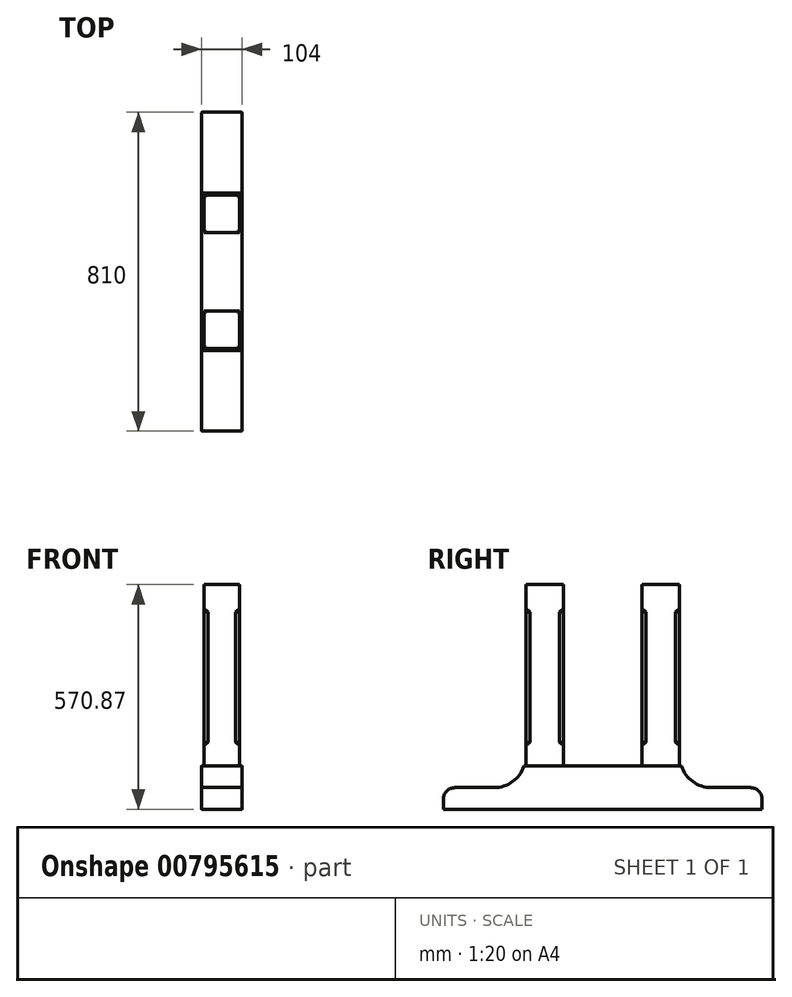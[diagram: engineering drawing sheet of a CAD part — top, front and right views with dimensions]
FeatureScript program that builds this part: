
annotation { "Feature Type Name" : "Feature", "Feature Type Description" : "" }
export const myFeature = defineFeature(function(context is Context, id is Id, definition is map)
    precondition{}
    {
        {
            var Q0;
            Q0=qCreatedBy(makeId("Right.planeOp"),FACE);
            var sketch = newSketch(context, id + "F0", { "sketchPlane" : qUnion([Q0])});
            skLineSegment(sketch, "E0", {"start": v(-405, 0) * mm, "end": v(-405, 55) * mm});
            skLineSegment(sketch, "E1", {"start": v(-405, 55) * mm, "end": v(-200, 55) * mm});
            skLineSegment(sketch, "E2", {"start": v(-200, 55) * mm, "end": v(-200, 110) * mm});
            skLineSegment(sketch, "E3", {"start": v(-200, 110) * mm, "end": v(-195, 110) * mm});
            skLineSegment(sketch, "E4", {"start": v(-195, 110) * mm, "end": v(-195, 570.87) * mm});
            skLineSegment(sketch, "E5", {"start": v(-195, 570.87) * mm, "end": v(-100, 570.87) * mm});
            skLineSegment(sketch, "E6", {"start": v(-100, 570.87) * mm, "end": v(-100, 110) * mm});
            skLineSegment(sketch, "E7", {"start": v(-100, 110) * mm, "end": v(0, 110) * mm});
            skLineSegment(sketch, "E8.MirrorCS", {"start": v(405, 0) * mm, "end": v(405, 55) * mm});
            skLineSegment(sketch, "E9.MirrorCS", {"start": v(405, 55) * mm, "end": v(200, 55) * mm});
            skLineSegment(sketch, "E10.MirrorCS", {"start": v(200, 110) * mm, "end": v(195, 110) * mm});
            skLineSegment(sketch, "E11.MirrorCS", {"start": v(195, 110) * mm, "end": v(195, 570.87) * mm});
            skLineSegment(sketch, "E12.MirrorCS", {"start": v(195, 570.87) * mm, "end": v(100, 570.87) * mm});
            skLineSegment(sketch, "E13.MirrorCS", {"start": v(100, 570.87) * mm, "end": v(100, 110) * mm});
            skLineSegment(sketch, "E14.MirrorCS", {"start": v(100, 110) * mm, "end": v(0, 110) * mm});
            skLineSegment(sketch, "E15.MirrorCS", {"start": v(200, 55) * mm, "end": v(200, 110) * mm});
            skLineSegment(sketch, "E16", {"start": v(-405, 0) * mm, "end": v(405, 0) * mm});
            skLineSegment(sketch, "E17", {"start": v(-195, 110) * mm, "end": v(-100, 110) * mm});
            skLineSegment(sketch, "E18", {"start": v(100, 110) * mm, "end": v(195, 110) * mm});
            skSolve(sketch);
        }
        {
            var Q0;
            Q0=makeQuery(id+"F0.imprint","IMPRINT",FACE,{"disambiguationData":[TD([[makeQuery(id+"F0.imprint","IMPRINT",EDGE,{"derivedFrom":sQuery(id+"F0.wireOp",EDGE,"E0")}),-1.0]])]});
            extrude(context, id + "F1", {"entities" : qUnion([Q0]), "depth" : 52 * mm, "offsetDistance" : 25 * mm, "hasSecondDirection" : true, "secondDirectionOppositeDirection" : true, "secondDirectionDepth" : 52 * mm});
        }
        {
            var Q0;
            Q0=makeQuery(id+"F0.imprint","IMPRINT",FACE,{"disambiguationData":[TD([[makeQuery(id+"F0.imprint","IMPRINT",EDGE,{"derivedFrom":sQuery(id+"F0.wireOp",EDGE,"E4")}),-1.0]])]});
            var Q1;
            Q1=makeQuery(id+"F0.imprint","IMPRINT",FACE,{"disambiguationData":[TD([[makeQuery(id+"F0.imprint","IMPRINT",EDGE,{"derivedFrom":sQuery(id+"F0.wireOp",EDGE,"E11.MirrorCS")}),1.0]])]});
            extrude(context, id + "F2", {"entities" : qUnion([Q0, Q1]), "operationType" : NewBodyOperationType.ADD, "oppositeDirection" : true, "depth" : 45 * mm, "offsetDistance" : 25 * mm, "hasSecondDirection" : true, "secondDirectionOppositeDirection" : false, "secondDirectionDepth" : 45 * mm});
        }
        {
            var Q0;
            Q0=makeQuery(id+"F1.opExtrude","SWEPT_EDGE",EDGE,{"disambiguationData":[OSD([sQuery(id+"F0.wireOp",EDGE,"E9.MirrorCS"),sQuery(id+"F0.wireOp",EDGE,"E8.MirrorCS")])]});
            var Q1;
            Q1=makeQuery(id+"F1.opExtrude","SWEPT_EDGE",EDGE,{"disambiguationData":[OSD([sQuery(id+"F0.wireOp",EDGE,"E0"),sQuery(id+"F0.wireOp",EDGE,"E1")])]});
            fillet(context, id + "F3", {"entities" : qUnion([Q0, Q1]), "radius" : 30 * mm, "tangentPropagation" : true, "allowEdgeOverflow" : false});
        }
        {
            var Q0;
            Q0=makeQuery(id+"F1.opExtrude","SWEPT_EDGE",EDGE,{"disambiguationData":[OSD([sQuery(id+"F0.wireOp",EDGE,"E9.MirrorCS"),sQuery(id+"F0.wireOp",EDGE,"E15.MirrorCS")])]});
            fillet(context, id + "F4", {"entities" : qUnion([Q0]), "radius" : 80 * mm, "tangentPropagation" : true, "allowEdgeOverflow" : false});
        }
        {
            var Q0;
            Q0=makeQuery(id+"F1.opExtrude","SWEPT_EDGE",EDGE,{"disambiguationData":[OSD([sQuery(id+"F0.wireOp",EDGE,"E1"),sQuery(id+"F0.wireOp",EDGE,"E2")])]});
            fillet(context, id + "F5", {"entities" : qUnion([Q0]), "radius" : 80 * mm, "tangentPropagation" : true, "allowEdgeOverflow" : false});
        }
        {
            var Q0;
            Q0=makeQuery(id+"F2.opExtrude","CAP_EDGE",EDGE,{"disambiguationData":[OSD([sQuery(id+"F0.wireOp",EDGE,"E4")])],"isStart":true});
            var Q1;
            Q1=makeQuery(id+"F2.opExtrude","CAP_EDGE",EDGE,{"disambiguationData":[OSD([sQuery(id+"F0.wireOp",EDGE,"E6")])],"isStart":true});
            var Q2;
            Q2=makeQuery(id+"F2.opExtrude","CAP_EDGE",EDGE,{"disambiguationData":[OSD([sQuery(id+"F0.wireOp",EDGE,"E13.MirrorCS")])],"isStart":true});
            var Q3;
            Q3=makeQuery(id+"F2.opExtrude","CAP_EDGE",EDGE,{"disambiguationData":[OSD([sQuery(id+"F0.wireOp",EDGE,"E4")])],"isStart":false});
            var Q4;
            Q4=makeQuery(id+"F2.opExtrude","CAP_EDGE",EDGE,{"disambiguationData":[OSD([sQuery(id+"F0.wireOp",EDGE,"E6")])],"isStart":false});
            var Q5;
            Q5=makeQuery(id+"F2.opExtrude","CAP_EDGE",EDGE,{"disambiguationData":[OSD([sQuery(id+"F0.wireOp",EDGE,"E13.MirrorCS")])],"isStart":false});
            var Q6;
            Q6=makeQuery(id+"F2.opExtrude","CAP_EDGE",EDGE,{"disambiguationData":[OSD([sQuery(id+"F0.wireOp",EDGE,"E11.MirrorCS")])],"isStart":false});
            var Q7;
            Q7=makeQuery(id+"F2.opExtrude","CAP_EDGE",EDGE,{"disambiguationData":[OSD([sQuery(id+"F0.wireOp",EDGE,"E11.MirrorCS")])],"isStart":true});
            chamfer(context, id + "F6", {"entities" : qUnion([Q0, Q1, Q2, Q3, Q4, Q5, Q6, Q7]), "width" : 10 * mm, "tangentPropagation" : true});
        }
        {
            var Q0;
            Q0=makeQuery(id+"F1.opExtrude","SWEPT_FACE",FACE,{"disambiguationData":[OSD([sQuery(id+"F0.wireOp",EDGE,"E3"),sQuery(id+"F0.wireOp",EDGE,"E7"),sQuery(id+"F0.wireOp",EDGE,"E10.MirrorCS"),sQuery(id+"F0.wireOp",EDGE,"E14.MirrorCS"),sQuery(id+"F0.wireOp",EDGE,"E17"),sQuery(id+"F0.wireOp",EDGE,"E18")])]});
            var sketch = newSketch(context, id + "F7", { "sketchPlane" : qUnion([Q0])});
            skLineSegment(sketch, "E19.bottom", {"start": v(-45, -195) * mm, "end": v(45, -195) * mm});
            skLineSegment(sketch, "E19.top", {"start": v(-45, -100) * mm, "end": v(45, -100) * mm});
            skLineSegment(sketch, "E19.left", {"start": v(-45, -195) * mm, "end": v(-45, -100) * mm});
            skLineSegment(sketch, "E19.right", {"start": v(45, -195) * mm, "end": v(45, -100) * mm});
            skLineSegment(sketch, "E20.bottom", {"start": v(-45, 100) * mm, "end": v(45, 100) * mm});
            skLineSegment(sketch, "E20.top", {"start": v(-45, 195) * mm, "end": v(45, 195) * mm});
            skLineSegment(sketch, "E20.left", {"start": v(-45, 100) * mm, "end": v(-45, 195) * mm});
            skLineSegment(sketch, "E20.right", {"start": v(45, 100) * mm, "end": v(45, 195) * mm});
            skSolve(sketch);
        }
        {
            var Q0;
            Q0 = qSketchRegion(id + "F7", true);
            extrude(context, id + "F8", {"entities" : qUnion([Q0]), "operationType" : NewBodyOperationType.ADD, "depth" : 50 * mm, "offsetDistance" : 25 * mm});
        }
        {
            var Q0;
            Q0=makeQuery(id+"F2.opExtrude","SWEPT_FACE",FACE,{"disambiguationData":[OSD([sQuery(id+"F0.wireOp",EDGE,"E5")])]});
            var sketch = newSketch(context, id + "F9", { "sketchPlane" : qUnion([Q0])});
            skLineSegment(sketch, "E21.bottom", {"start": v(45, 195) * mm, "end": v(-45, 195) * mm});
            skLineSegment(sketch, "E21.top", {"start": v(45, 100) * mm, "end": v(-45, 100) * mm});
            skLineSegment(sketch, "E21.left", {"start": v(45, 195) * mm, "end": v(45, 100) * mm});
            skLineSegment(sketch, "E21.right", {"start": v(-45, 195) * mm, "end": v(-45, 100) * mm});
            skPoint(sketch, "E22.firstSnap0", {"position": v(45, -147.5) * mm});
            skLineSegment(sketch, "E22.bottom", {"start": v(45, -100) * mm, "end": v(-45, -100) * mm});
            skLineSegment(sketch, "E22.top", {"start": v(45, -195) * mm, "end": v(-45, -195) * mm});
            skLineSegment(sketch, "E22.left", {"start": v(45, -100) * mm, "end": v(45, -195) * mm});
            skLineSegment(sketch, "E22.right", {"start": v(-45, -100) * mm, "end": v(-45, -195) * mm});
            skSolve(sketch);
        }
        {
            var Q0;
            {var subQ1=makeQuery(id+"F6.opChamfer","BLEND_EDGE",EDGE,{"blendedFrom":[makeQuery(id+"F2.opExtrude","CAP_EDGE",EDGE,{"disambiguationData":[OSD([sQuery(id+"F0.wireOp",EDGE,"E6")])],"isStart":true}),makeQuery(id+"F2.opExtrude","SWEPT_FACE",FACE,{"disambiguationData":[OSD([sQuery(id+"F0.wireOp",EDGE,"E5")])]})],"blendedInto":[makeQuery(id+"F2.opExtrude","SWEPT_FACE",FACE,{"disambiguationData":[OSD([sQuery(id+"F0.wireOp",EDGE,"E5")])]})]});Q0=makeQuery(id+"F9.imprint","IMPRINT",FACE,{"disambiguationData":[TD([[makeQuery(id+"F9.imprint","IMPRINT",EDGE,{"derivedFrom":subQ1}),-1.0]])]});}
            var Q1;
            {var subQ1=makeQuery(id+"F6.opChamfer","BLEND_EDGE",EDGE,{"blendedFrom":[makeQuery(id+"F2.opExtrude","CAP_EDGE",EDGE,{"disambiguationData":[OSD([sQuery(id+"F0.wireOp",EDGE,"E6")])],"isStart":false}),makeQuery(id+"F2.opExtrude","SWEPT_FACE",FACE,{"disambiguationData":[OSD([sQuery(id+"F0.wireOp",EDGE,"E5")])]})],"blendedInto":[makeQuery(id+"F2.opExtrude","SWEPT_FACE",FACE,{"disambiguationData":[OSD([sQuery(id+"F0.wireOp",EDGE,"E5")])]})]});Q1=makeQuery(id+"F9.imprint","IMPRINT",FACE,{"disambiguationData":[TD([[makeQuery(id+"F9.imprint","IMPRINT",EDGE,{"derivedFrom":subQ1}),-1.0]])]});}
            var Q2;
            {var subQ1=makeQuery(id+"F6.opChamfer","BLEND_EDGE",EDGE,{"blendedFrom":[makeQuery(id+"F2.opExtrude","CAP_EDGE",EDGE,{"disambiguationData":[OSD([sQuery(id+"F0.wireOp",EDGE,"E4")])],"isStart":true}),makeQuery(id+"F2.opExtrude","SWEPT_FACE",FACE,{"disambiguationData":[OSD([sQuery(id+"F0.wireOp",EDGE,"E5")])]})],"blendedInto":[makeQuery(id+"F2.opExtrude","SWEPT_FACE",FACE,{"disambiguationData":[OSD([sQuery(id+"F0.wireOp",EDGE,"E5")])]})]});Q2=makeQuery(id+"F9.imprint","IMPRINT",FACE,{"disambiguationData":[TD([[makeQuery(id+"F9.imprint","IMPRINT",EDGE,{"derivedFrom":subQ1}),-1.0]])]});}
            var Q3;
            {var subQ1=makeQuery(id+"F6.opChamfer","BLEND_EDGE",EDGE,{"blendedFrom":[makeQuery(id+"F2.opExtrude","CAP_EDGE",EDGE,{"disambiguationData":[OSD([sQuery(id+"F0.wireOp",EDGE,"E4")])],"isStart":false}),makeQuery(id+"F2.opExtrude","SWEPT_FACE",FACE,{"disambiguationData":[OSD([sQuery(id+"F0.wireOp",EDGE,"E5")])]})],"blendedInto":[makeQuery(id+"F2.opExtrude","SWEPT_FACE",FACE,{"disambiguationData":[OSD([sQuery(id+"F0.wireOp",EDGE,"E5")])]})]});Q3=makeQuery(id+"F9.imprint","IMPRINT",FACE,{"disambiguationData":[TD([[makeQuery(id+"F9.imprint","IMPRINT",EDGE,{"derivedFrom":subQ1}),-1.0]])]});}
            var Q4;
            Q4=makeQuery(id+"F9.imprint","IMPRINT",FACE,{"disambiguationData":[TD([[makeQuery(id+"F9.imprint","IMPRINT",EDGE,{"derivedFrom":sQuery(id+"F9.wireOp",EDGE,"E21.bottom")}),1.0]])]});
            var Q5;
            {var subQ1=makeQuery(id+"F2.opExtrude","SWEPT_FACE",FACE,{"disambiguationData":[OSD([sQuery(id+"F0.wireOp",EDGE,"E5")])]});var subQ2=sQuery(id+"F0.wireOp",EDGE,"E4");var subQ7=makeQuery(id+"F6.opChamfer","BLEND_EDGE",EDGE,{"blendedFrom":[makeQuery(id+"F2.opExtrude","CAP_EDGE",EDGE,{"disambiguationData":[OSD([subQ2])],"isStart":true}),subQ1],"blendedInto":[subQ1]});Q5=makeQuery(id+"F9.imprint","IMPRINT",FACE,{"disambiguationData":[TD([[makeQuery(id+"F9.imprint","IMPRINT",EDGE,{"derivedFrom":subQ7}),1.0]])]});}
            extrude(context, id + "F10", {"entities" : qUnion([Q0, Q1, Q2, Q3, Q4, Q5]), "operationType" : NewBodyOperationType.ADD, "oppositeDirection" : true, "depth" : 60 * mm, "offsetDistance" : 25 * mm});
        }
        {
            var Q0;
            {var subQ0=sQuery(id+"F0.wireOp",EDGE,"E4");Q0=makeQuery(id+"F10.boolean.opBoolean","INTERSECT",EDGE,{"derivedFrom":[makeQuery(id+"F6.opChamfer","BLEND_FACE",FACE,{"disambiguationData":[OSD([subQ0]),TDD([makeQuery(id+"F2.opExtrude","CAP_EDGE",EDGE,{"disambiguationData":[OSD([subQ0])],"isStart":true})])]}),makeQuery(id+"F10.opExtrude","CAP_FACE",FACE,{"disambiguationData":[OSD([sQuery(id+"F9.wireOp",EDGE,"E22.bottom"),sQuery(id+"F9.wireOp",EDGE,"E22.top"),sQuery(id+"F9.wireOp",EDGE,"E22.left"),sQuery(id+"F9.wireOp",EDGE,"E22.right")])],"isStart":false})]});}
            var Q1;
            {var subQ0=sQuery(id+"F0.wireOp",EDGE,"E6");Q1=makeQuery(id+"F10.boolean.opBoolean","INTERSECT",EDGE,{"derivedFrom":[makeQuery(id+"F6.opChamfer","BLEND_FACE",FACE,{"disambiguationData":[OSD([subQ0]),TDD([makeQuery(id+"F2.opExtrude","CAP_EDGE",EDGE,{"disambiguationData":[OSD([subQ0])],"isStart":true})])]}),makeQuery(id+"F10.opExtrude","CAP_FACE",FACE,{"disambiguationData":[OSD([sQuery(id+"F9.wireOp",EDGE,"E22.bottom"),sQuery(id+"F9.wireOp",EDGE,"E22.top"),sQuery(id+"F9.wireOp",EDGE,"E22.left"),sQuery(id+"F9.wireOp",EDGE,"E22.right")])],"isStart":false})]});}
            var Q2;
            {var subQ0=sQuery(id+"F0.wireOp",EDGE,"E6");Q2=makeQuery(id+"F10.boolean.opBoolean","INTERSECT",EDGE,{"derivedFrom":[makeQuery(id+"F6.opChamfer","BLEND_FACE",FACE,{"disambiguationData":[OSD([subQ0]),TDD([makeQuery(id+"F2.opExtrude","CAP_EDGE",EDGE,{"disambiguationData":[OSD([subQ0])],"isStart":false})])]}),makeQuery(id+"F10.opExtrude","CAP_FACE",FACE,{"disambiguationData":[OSD([sQuery(id+"F9.wireOp",EDGE,"E22.bottom"),sQuery(id+"F9.wireOp",EDGE,"E22.top"),sQuery(id+"F9.wireOp",EDGE,"E22.left"),sQuery(id+"F9.wireOp",EDGE,"E22.right")])],"isStart":false})]});}
            var Q3;
            {var subQ0=sQuery(id+"F0.wireOp",EDGE,"E4");Q3=makeQuery(id+"F10.boolean.opBoolean","INTERSECT",EDGE,{"derivedFrom":[makeQuery(id+"F6.opChamfer","BLEND_FACE",FACE,{"disambiguationData":[OSD([subQ0]),TDD([makeQuery(id+"F2.opExtrude","CAP_EDGE",EDGE,{"disambiguationData":[OSD([subQ0])],"isStart":false})])]}),makeQuery(id+"F10.opExtrude","CAP_FACE",FACE,{"disambiguationData":[OSD([sQuery(id+"F9.wireOp",EDGE,"E22.bottom"),sQuery(id+"F9.wireOp",EDGE,"E22.top"),sQuery(id+"F9.wireOp",EDGE,"E22.left"),sQuery(id+"F9.wireOp",EDGE,"E22.right")])],"isStart":false})]});}
            var Q4;
            {var subQ0=sQuery(id+"F0.wireOp",EDGE,"E11.MirrorCS");Q4=makeQuery(id+"F10.boolean.opBoolean","INTERSECT",EDGE,{"derivedFrom":[makeQuery(id+"F6.opChamfer","BLEND_FACE",FACE,{"disambiguationData":[OSD([subQ0]),TDD([makeQuery(id+"F2.opExtrude","CAP_EDGE",EDGE,{"disambiguationData":[OSD([subQ0])],"isStart":true})])]}),makeQuery(id+"F10.opExtrude","CAP_FACE",FACE,{"disambiguationData":[OSD([sQuery(id+"F9.wireOp",EDGE,"E21.bottom"),sQuery(id+"F9.wireOp",EDGE,"E21.top"),sQuery(id+"F9.wireOp",EDGE,"E21.left"),sQuery(id+"F9.wireOp",EDGE,"E21.right")])],"isStart":false})]});}
            var Q5;
            {var subQ0=sQuery(id+"F0.wireOp",EDGE,"E13.MirrorCS");Q5=makeQuery(id+"F10.boolean.opBoolean","INTERSECT",EDGE,{"derivedFrom":[makeQuery(id+"F6.opChamfer","BLEND_FACE",FACE,{"disambiguationData":[OSD([subQ0]),TDD([makeQuery(id+"F2.opExtrude","CAP_EDGE",EDGE,{"disambiguationData":[OSD([subQ0])],"isStart":true})])]}),makeQuery(id+"F10.opExtrude","CAP_FACE",FACE,{"disambiguationData":[OSD([sQuery(id+"F9.wireOp",EDGE,"E21.bottom"),sQuery(id+"F9.wireOp",EDGE,"E21.top"),sQuery(id+"F9.wireOp",EDGE,"E21.left"),sQuery(id+"F9.wireOp",EDGE,"E21.right")])],"isStart":false})]});}
            var Q6;
            {var subQ0=sQuery(id+"F0.wireOp",EDGE,"E13.MirrorCS");Q6=makeQuery(id+"F10.boolean.opBoolean","INTERSECT",EDGE,{"derivedFrom":[makeQuery(id+"F6.opChamfer","BLEND_FACE",FACE,{"disambiguationData":[OSD([subQ0]),TDD([makeQuery(id+"F2.opExtrude","CAP_EDGE",EDGE,{"disambiguationData":[OSD([subQ0])],"isStart":false})])]}),makeQuery(id+"F10.opExtrude","CAP_FACE",FACE,{"disambiguationData":[OSD([sQuery(id+"F9.wireOp",EDGE,"E21.bottom"),sQuery(id+"F9.wireOp",EDGE,"E21.top"),sQuery(id+"F9.wireOp",EDGE,"E21.left"),sQuery(id+"F9.wireOp",EDGE,"E21.right")])],"isStart":false})]});}
            var Q7;
            {var subQ0=sQuery(id+"F0.wireOp",EDGE,"E11.MirrorCS");Q7=makeQuery(id+"F10.boolean.opBoolean","INTERSECT",EDGE,{"derivedFrom":[makeQuery(id+"F6.opChamfer","BLEND_FACE",FACE,{"disambiguationData":[OSD([subQ0]),TDD([makeQuery(id+"F2.opExtrude","CAP_EDGE",EDGE,{"disambiguationData":[OSD([subQ0])],"isStart":false})])]}),makeQuery(id+"F10.opExtrude","CAP_FACE",FACE,{"disambiguationData":[OSD([sQuery(id+"F9.wireOp",EDGE,"E21.bottom"),sQuery(id+"F9.wireOp",EDGE,"E21.top"),sQuery(id+"F9.wireOp",EDGE,"E21.left"),sQuery(id+"F9.wireOp",EDGE,"E21.right")])],"isStart":false})]});}
            chamfer(context, id + "F11", {"entities" : qUnion([Q0, Q1, Q2, Q3, Q4, Q5, Q6, Q7]), "width" : 10 * mm, "tangentPropagation" : true});
        }
        {
            var Q0;
            {var subQ0=sQuery(id+"F0.wireOp",EDGE,"E11.MirrorCS");Q0=makeQuery(id+"F8.boolean.opBoolean","INTERSECT",EDGE,{"derivedFrom":[makeQuery(id+"F6.opChamfer","BLEND_FACE",FACE,{"disambiguationData":[OSD([subQ0]),TDD([makeQuery(id+"F2.opExtrude","CAP_EDGE",EDGE,{"disambiguationData":[OSD([subQ0])],"isStart":false})])]}),makeQuery(id+"F8.opExtrude","CAP_FACE",FACE,{"disambiguationData":[OSD([sQuery(id+"F7.wireOp",EDGE,"E20.bottom"),sQuery(id+"F7.wireOp",EDGE,"E20.top"),sQuery(id+"F7.wireOp",EDGE,"E20.left"),sQuery(id+"F7.wireOp",EDGE,"E20.right")])],"isStart":false})]});}
            var Q1;
            {var subQ0=sQuery(id+"F0.wireOp",EDGE,"E11.MirrorCS");Q1=makeQuery(id+"F8.boolean.opBoolean","INTERSECT",EDGE,{"derivedFrom":[makeQuery(id+"F6.opChamfer","BLEND_FACE",FACE,{"disambiguationData":[OSD([subQ0]),TDD([makeQuery(id+"F2.opExtrude","CAP_EDGE",EDGE,{"disambiguationData":[OSD([subQ0])],"isStart":true})])]}),makeQuery(id+"F8.opExtrude","CAP_FACE",FACE,{"disambiguationData":[OSD([sQuery(id+"F7.wireOp",EDGE,"E20.bottom"),sQuery(id+"F7.wireOp",EDGE,"E20.top"),sQuery(id+"F7.wireOp",EDGE,"E20.left"),sQuery(id+"F7.wireOp",EDGE,"E20.right")])],"isStart":false})]});}
            var Q2;
            {var subQ0=sQuery(id+"F0.wireOp",EDGE,"E13.MirrorCS");Q2=makeQuery(id+"F8.boolean.opBoolean","INTERSECT",EDGE,{"derivedFrom":[makeQuery(id+"F6.opChamfer","BLEND_FACE",FACE,{"disambiguationData":[OSD([subQ0]),TDD([makeQuery(id+"F2.opExtrude","CAP_EDGE",EDGE,{"disambiguationData":[OSD([subQ0])],"isStart":true})])]}),makeQuery(id+"F8.opExtrude","CAP_FACE",FACE,{"disambiguationData":[OSD([sQuery(id+"F7.wireOp",EDGE,"E20.bottom"),sQuery(id+"F7.wireOp",EDGE,"E20.top"),sQuery(id+"F7.wireOp",EDGE,"E20.left"),sQuery(id+"F7.wireOp",EDGE,"E20.right")])],"isStart":false})]});}
            var Q3;
            {var subQ0=sQuery(id+"F0.wireOp",EDGE,"E4");Q3=makeQuery(id+"F8.boolean.opBoolean","INTERSECT",EDGE,{"derivedFrom":[makeQuery(id+"F6.opChamfer","BLEND_FACE",FACE,{"disambiguationData":[OSD([subQ0]),TDD([makeQuery(id+"F2.opExtrude","CAP_EDGE",EDGE,{"disambiguationData":[OSD([subQ0])],"isStart":true})])]}),makeQuery(id+"F8.opExtrude","CAP_FACE",FACE,{"disambiguationData":[OSD([sQuery(id+"F7.wireOp",EDGE,"E19.bottom"),sQuery(id+"F7.wireOp",EDGE,"E19.top"),sQuery(id+"F7.wireOp",EDGE,"E19.left"),sQuery(id+"F7.wireOp",EDGE,"E19.right")])],"isStart":false})]});}
            var Q4;
            {var subQ0=sQuery(id+"F0.wireOp",EDGE,"E6");Q4=makeQuery(id+"F8.boolean.opBoolean","INTERSECT",EDGE,{"derivedFrom":[makeQuery(id+"F6.opChamfer","BLEND_FACE",FACE,{"disambiguationData":[OSD([subQ0]),TDD([makeQuery(id+"F2.opExtrude","CAP_EDGE",EDGE,{"disambiguationData":[OSD([subQ0])],"isStart":true})])]}),makeQuery(id+"F8.opExtrude","CAP_FACE",FACE,{"disambiguationData":[OSD([sQuery(id+"F7.wireOp",EDGE,"E19.bottom"),sQuery(id+"F7.wireOp",EDGE,"E19.top"),sQuery(id+"F7.wireOp",EDGE,"E19.left"),sQuery(id+"F7.wireOp",EDGE,"E19.right")])],"isStart":false})]});}
            var Q5;
            {var subQ0=sQuery(id+"F0.wireOp",EDGE,"E6");Q5=makeQuery(id+"F8.boolean.opBoolean","INTERSECT",EDGE,{"derivedFrom":[makeQuery(id+"F6.opChamfer","BLEND_FACE",FACE,{"disambiguationData":[OSD([subQ0]),TDD([makeQuery(id+"F2.opExtrude","CAP_EDGE",EDGE,{"disambiguationData":[OSD([subQ0])],"isStart":false})])]}),makeQuery(id+"F8.opExtrude","CAP_FACE",FACE,{"disambiguationData":[OSD([sQuery(id+"F7.wireOp",EDGE,"E19.bottom"),sQuery(id+"F7.wireOp",EDGE,"E19.top"),sQuery(id+"F7.wireOp",EDGE,"E19.left"),sQuery(id+"F7.wireOp",EDGE,"E19.right")])],"isStart":false})]});}
            var Q6;
            {var subQ0=sQuery(id+"F0.wireOp",EDGE,"E13.MirrorCS");Q6=makeQuery(id+"F8.boolean.opBoolean","INTERSECT",EDGE,{"derivedFrom":[makeQuery(id+"F6.opChamfer","BLEND_FACE",FACE,{"disambiguationData":[OSD([subQ0]),TDD([makeQuery(id+"F2.opExtrude","CAP_EDGE",EDGE,{"disambiguationData":[OSD([subQ0])],"isStart":false})])]}),makeQuery(id+"F8.opExtrude","CAP_FACE",FACE,{"disambiguationData":[OSD([sQuery(id+"F7.wireOp",EDGE,"E20.bottom"),sQuery(id+"F7.wireOp",EDGE,"E20.top"),sQuery(id+"F7.wireOp",EDGE,"E20.left"),sQuery(id+"F7.wireOp",EDGE,"E20.right")])],"isStart":false})]});}
            var Q7;
            {var subQ0=sQuery(id+"F0.wireOp",EDGE,"E4");Q7=makeQuery(id+"F8.boolean.opBoolean","INTERSECT",EDGE,{"derivedFrom":[makeQuery(id+"F6.opChamfer","BLEND_FACE",FACE,{"disambiguationData":[OSD([subQ0]),TDD([makeQuery(id+"F2.opExtrude","CAP_EDGE",EDGE,{"disambiguationData":[OSD([subQ0])],"isStart":false})])]}),makeQuery(id+"F8.opExtrude","CAP_FACE",FACE,{"disambiguationData":[OSD([sQuery(id+"F7.wireOp",EDGE,"E19.bottom"),sQuery(id+"F7.wireOp",EDGE,"E19.top"),sQuery(id+"F7.wireOp",EDGE,"E19.left"),sQuery(id+"F7.wireOp",EDGE,"E19.right")])],"isStart":false})]});}
            chamfer(context, id + "F12", {"entities" : qUnion([Q0, Q1, Q2, Q3, Q4, Q5, Q6, Q7]), "width" : 10 * mm, "tangentPropagation" : true});
        }
        {
            var Q0;
            Q0=makeQuery(id+"F1.opExtrude","CAP_FACE",FACE,{"disambiguationData":[OSD([sQuery(id+"F0.wireOp",EDGE,"E0"),sQuery(id+"F0.wireOp",EDGE,"E1"),sQuery(id+"F0.wireOp",EDGE,"E2"),sQuery(id+"F0.wireOp",EDGE,"E3"),sQuery(id+"F0.wireOp",EDGE,"E7"),sQuery(id+"F0.wireOp",EDGE,"E9.MirrorCS"),sQuery(id+"F0.wireOp",EDGE,"E10.MirrorCS"),sQuery(id+"F0.wireOp",EDGE,"E14.MirrorCS"),sQuery(id+"F0.wireOp",EDGE,"E15.MirrorCS"),sQuery(id+"F0.wireOp",EDGE,"E8.MirrorCS"),sQuery(id+"F0.wireOp",EDGE,"E16"),sQuery(id+"F0.wireOp",EDGE,"E17"),sQuery(id+"F0.wireOp",EDGE,"E18")])],"isStart":false});
            var Q1;
            Q1=makeQuery(id+"F1.opExtrude","CAP_FACE",FACE,{"disambiguationData":[OSD([sQuery(id+"F0.wireOp",EDGE,"E0"),sQuery(id+"F0.wireOp",EDGE,"E1"),sQuery(id+"F0.wireOp",EDGE,"E2"),sQuery(id+"F0.wireOp",EDGE,"E3"),sQuery(id+"F0.wireOp",EDGE,"E7"),sQuery(id+"F0.wireOp",EDGE,"E9.MirrorCS"),sQuery(id+"F0.wireOp",EDGE,"E10.MirrorCS"),sQuery(id+"F0.wireOp",EDGE,"E14.MirrorCS"),sQuery(id+"F0.wireOp",EDGE,"E15.MirrorCS"),sQuery(id+"F0.wireOp",EDGE,"E8.MirrorCS"),sQuery(id+"F0.wireOp",EDGE,"E16"),sQuery(id+"F0.wireOp",EDGE,"E17"),sQuery(id+"F0.wireOp",EDGE,"E18")])],"isStart":true});
            fillet(context, id + "F13", {"entities" : qUnion([Q0, Q1]), "radius" : 2 * mm, "tangentPropagation" : true, "allowEdgeOverflow" : false});
        }
    });
